# Revit family: Haworth_BuzziFalls_Plain_AP_PRELIMINARY
name_source: partatom
category: Furniture
revit_build: Autodesk Revit 2018 (Build: 20170223_1515(x64)
units: mm (PartAtom-declared; Revit-internal decimal feet)

## family parameters
Always vertical = Yes
Cut with Voids When Loaded = No
OmniClass Number = 23.40.70.14.64.21
OmniClass Title = Systems Furniture
Room Calculation Point = No
Shared = No
Work Plane-Based = No

## types (2) — shared parameters
Actual Depth = 20 mm
Actual Width = 800 mm
Assembly Code = E2020200
Cable Length = 2000 mm  [stored 6.56168 ft]
Connector Finish = Haworth _ Paint _ Black BTR-9005
Description = Haworth - BuzziSpace - BuzziFalls - Screen
Manufacturer = Haworth
Model = BuzziFalls
Patterns = Plain, Alhambra, Birch, Dots, Grid, Leaves, Orient, Palms, Parrots, Pebbles, Rain, Royal, Tropics
Revision Number = 1
Size = Verify Final Dim. w/ Haworth
URL = https://www.haworth.com
URL - Product = https://www.haworth.com
Warranty = http://www.haworth.com

## per-type parameters (varying)
| type | Actual Height | Large | Small |
| Small Screen | 2200 mm | No | Yes |
| Large Screen | 2500 mm | Yes | No |

note: [stored X ft] marks values corroborated as IEEE doubles in the binary element streams (Revit-internal decimal feet)

## geometry (parser evidence)
native form markers: Sweep x2
no freeform markers — native parametric forms only
